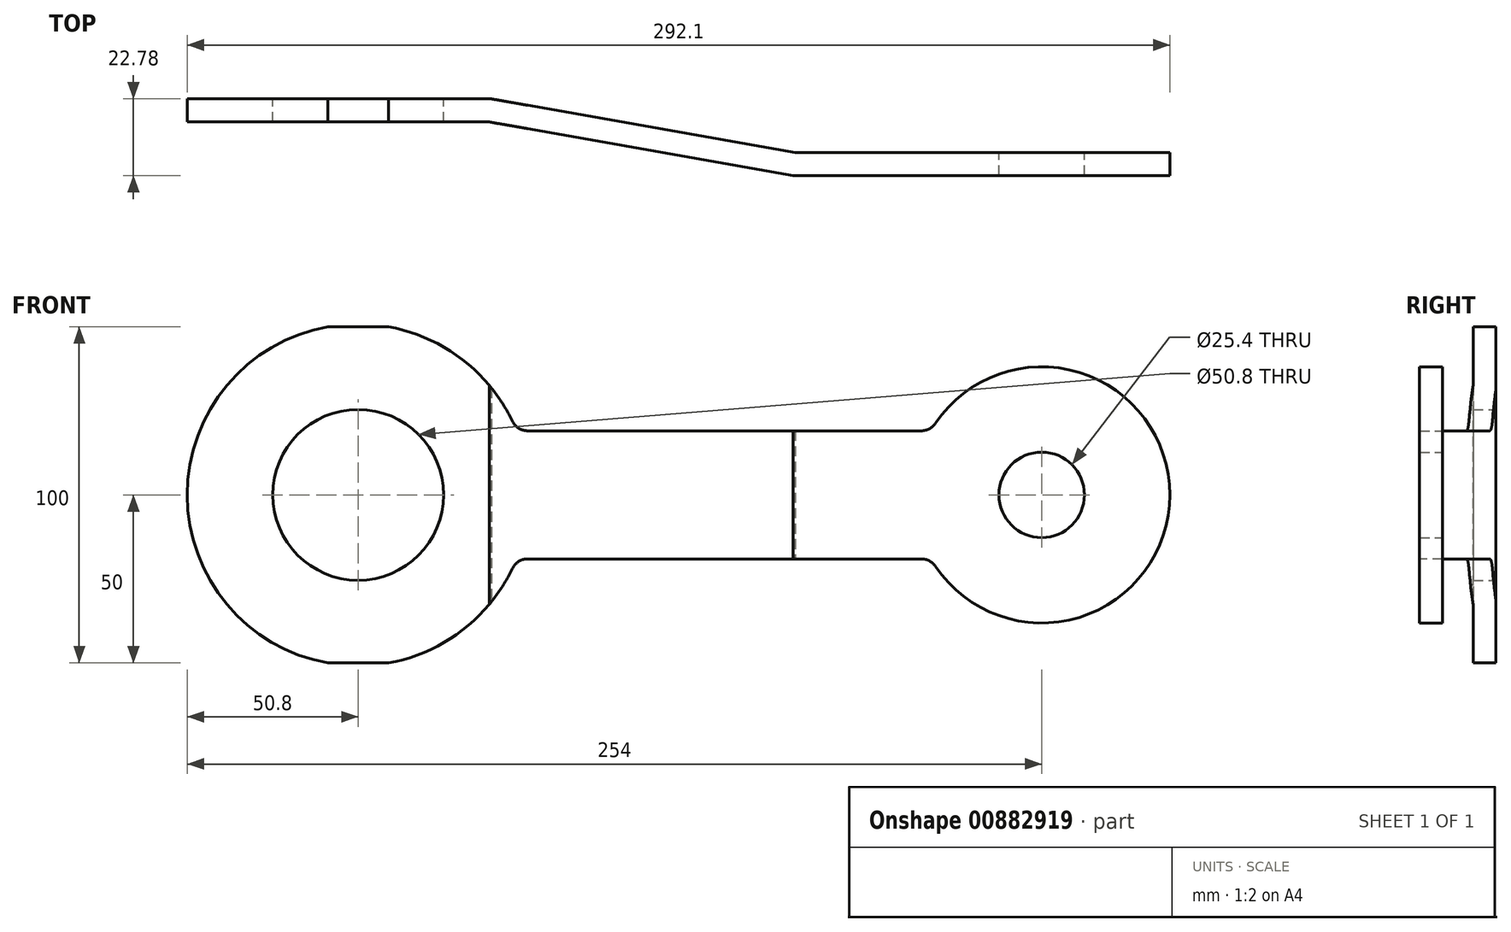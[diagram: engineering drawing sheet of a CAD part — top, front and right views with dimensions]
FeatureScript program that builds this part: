
annotation { "Feature Type Name" : "Feature", "Feature Type Description" : "" }
export const myFeature = defineFeature(function(context is Context, id is Id, definition is map)
    precondition{}
    {
        {
            var Q0;
            Q0=qCreatedBy(makeId("Front.planeOp"),FACE);
            var sketch = newSketch(context, id + "F0", { "sketchPlane" : qUnion([Q0])});
            skCircle(sketch, "E0", {"center": v(0, 0) * mm, "radius": 50.8 * mm});
            skCircle(sketch, "E1", {"center": v(203.2, 0) * mm, "radius": 38.1 * mm});
            skLineSegment(sketch, "E2", {"start": v(0, 0) * mm, "end": v(203.2, 0) * mm, "construction": true});
            skLineSegment(sketch, "E3", {"start": v(47.1, 19.05) * mm, "end": v(170.2, 19.05) * mm});
            skLineSegment(sketch, "E4.MirrorCS", {"start": v(47.1, -19.05) * mm, "end": v(170.2, -19.05) * mm});
            skCircle(sketch, "E5", {"center": v(0, 0) * mm, "radius": 25.4 * mm});
            skCircle(sketch, "E6", {"center": v(203.2, 0) * mm, "radius": 12.7 * mm});
            skSolve(sketch);
        }
        {
            var Q0;
            Q0=makeQuery(id+"F0.imprint","IMPRINT",FACE,{"disambiguationData":[TD([[makeQuery(id+"F0.imprint","IMPRINT",EDGE,{"derivedFrom":sQuery(id+"F0.wireOp",EDGE,"E5")}),-1.0]])]});
            var Q1;
            {var subQ0=sQuery(id+"F0.wireOp",EDGE,"E3");Q1=makeQuery(id+"F0.imprint","IMPRINT",FACE,{"disambiguationData":[TD([[makeQuery(id+"F0.imprint","IMPRINT",EDGE,{"derivedFrom":subQ0}),-1.0]])]});}
            var Q2;
            Q2=makeQuery(id+"F0.imprint","IMPRINT",FACE,{"disambiguationData":[TD([[makeQuery(id+"F0.imprint","IMPRINT",EDGE,{"derivedFrom":sQuery(id+"F0.wireOp",EDGE,"E6")}),-1.0]])]});
            extrude(context, id + "F1", {"entities" : qUnion([Q0, Q1, Q2]), "depth" : 25.4 * mm, "offsetDistance" : 25.4 * mm});
        }
        {
            var Q0;
            Q0=qCreatedBy(makeId("Top.planeOp"),FACE);
            var sketch = newSketch(context, id + "F2", { "sketchPlane" : qUnion([Q0])});
            skLineSegment(sketch, "E7", {"start": v(-68.86, 0) * mm, "end": v(39.6, 0) * mm});
            skLineSegment(sketch, "E8", {"start": v(39.6, 0) * mm, "end": v(129.9, -15.92) * mm});
            skLineSegment(sketch, "E9", {"start": v(129.9, -15.92) * mm, "end": v(255.29, -15.92) * mm});
            skLineSegment(sketch, "E10.0", {"start": v(129.3, -22.78) * mm, "end": v(255.29, -22.78) * mm});
            skLineSegment(sketch, "E10.1", {"start": v(39, -6.86) * mm, "end": v(129.3, -22.78) * mm});
            skLineSegment(sketch, "E10.2", {"start": v(-68.86, -6.86) * mm, "end": v(39, -6.86) * mm});
            skLineSegment(sketch, "E11", {"start": v(255.29, -22.78) * mm, "end": v(255.29, -15.92) * mm});
            skLineSegment(sketch, "E12", {"start": v(-68.86, 0) * mm, "end": v(-68.86, -6.86) * mm});
            skSolve(sketch);
        }
        {
            var Q0;
            Q0=makeQuery(id+"F2.imprint","IMPRINT",FACE,{"disambiguationData":[TD([[makeQuery(id+"F2.imprint","IMPRINT",EDGE,{"derivedFrom":sQuery(id+"F2.wireOp",EDGE,"E7")}),-1.0]])]});
            extrude(context, id + "F3", {"entities" : qUnion([Q0]), "operationType" : NewBodyOperationType.INTERSECT, "endBound" : BoundingType.SYMMETRIC, "depth" : 100 * mm, "offsetDistance" : 25.4 * mm});
        }
        {
            var Q0;
            Q0=makeQuery(id+"F3.boolean.opBoolean","COPY",EDGE,{"derivedFrom":makeQuery(id+"F3.boolean.toolComplement.opBoolean","COPY",EDGE,{"derivedFrom":makeQuery(id+"F3.opExtrude","SWEPT_EDGE",EDGE,{"disambiguationData":[OSD([sQuery(id+"F2.wireOp",EDGE,"E8"),sQuery(id+"F2.wireOp",EDGE,"E9")])]})})});
            var Q1;
            Q1=makeQuery(id+"F3.boolean.opBoolean","COPY",EDGE,{"derivedFrom":makeQuery(id+"F3.boolean.toolComplement.opBoolean","COPY",EDGE,{"derivedFrom":makeQuery(id+"F3.opExtrude","SWEPT_EDGE",EDGE,{"disambiguationData":[OSD([sQuery(id+"F2.wireOp",EDGE,"E7"),sQuery(id+"F2.wireOp",EDGE,"E8")])]})})});
            var Q2;
            Q2=makeQuery(id+"F3.boolean.opBoolean","COPY",EDGE,{"derivedFrom":makeQuery(id+"F3.boolean.toolComplement.opBoolean","COPY",EDGE,{"derivedFrom":makeQuery(id+"F3.opExtrude","SWEPT_EDGE",EDGE,{"disambiguationData":[OSD([sQuery(id+"F2.wireOp",EDGE,"E10.1"),sQuery(id+"F2.wireOp",EDGE,"E10.2")])]})})});
            var Q3;
            Q3=makeQuery(id+"F3.boolean.opBoolean","COPY",EDGE,{"derivedFrom":makeQuery(id+"F3.boolean.toolComplement.opBoolean","COPY",EDGE,{"derivedFrom":makeQuery(id+"F3.opExtrude","SWEPT_EDGE",EDGE,{"disambiguationData":[OSD([sQuery(id+"F2.wireOp",EDGE,"E10.0"),sQuery(id+"F2.wireOp",EDGE,"E10.1")])]})})});
            var Q4;
            Q4=makeQuery(id+"F1.opExtrude","SWEPT_EDGE",EDGE,{"disambiguationData":[OSD([sQuery(id+"F0.wireOp",EDGE,"E0"),sQuery(id+"F0.wireOp",EDGE,"E3")])]});
            var Q5;
            Q5=makeQuery(id+"F1.opExtrude","SWEPT_EDGE",EDGE,{"disambiguationData":[OSD([sQuery(id+"F0.wireOp",EDGE,"E1"),sQuery(id+"F0.wireOp",EDGE,"E3")])]});
            var Q6;
            Q6=makeQuery(id+"F1.opExtrude","SWEPT_EDGE",EDGE,{"disambiguationData":[OSD([sQuery(id+"F0.wireOp",EDGE,"E1"),sQuery(id+"F0.wireOp",EDGE,"E4.MirrorCS")])]});
            var Q7;
            Q7=makeQuery(id+"F1.opExtrude","SWEPT_EDGE",EDGE,{"disambiguationData":[OSD([sQuery(id+"F0.wireOp",EDGE,"E0"),sQuery(id+"F0.wireOp",EDGE,"E4.MirrorCS")])]});
            fillet(context, id + "F4", {"entities" : qUnion([Q0, Q1, Q2, Q3, Q4, Q5, Q6, Q7]), "radius" : 5.08 * mm, "tangentPropagation" : true, "allowEdgeOverflow" : false});
        }
    });
